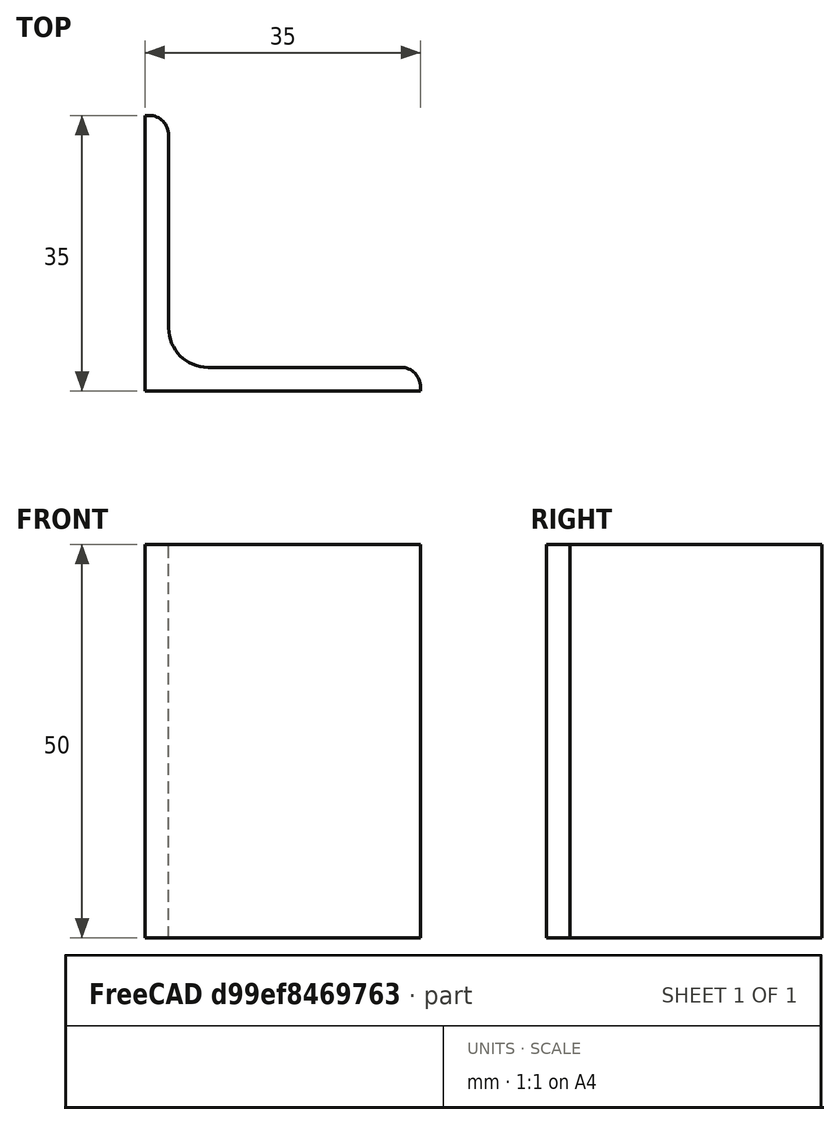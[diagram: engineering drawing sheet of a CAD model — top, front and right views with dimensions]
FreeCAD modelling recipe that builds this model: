
FCSTD DOCUMENT  (FreeCAD 0.15R4671 (Git))
Label: Angle Bar L35x35x3 EN10056 S235JR
License: All rights reserved
LicenseURL: http://en.wikipedia.org/wiki/All_rights_reserved
objects: Sketcher::SketchObject×1, Part::Extrusion×1
note: 2 computed .brp shape members not serialized (recipe doc carries the construction recipe); baked Part::Feature solids carry a one-line shape summary decoded from their .brp

FEATURE [Sketcher::SketchObject] Sketch
  sketch-geometry (9):
    g0: LineSegment StartX=0 StartY=0 StartZ=0 EndX=35 EndY=0 EndZ=0
    g1: LineSegment StartX=35 StartY=0 StartZ=0 EndX=35 EndY=0.5 EndZ=0
    g2: LineSegment StartX=32.5 StartY=3 StartZ=0 EndX=8 EndY=3 EndZ=0
    g3: LineSegment StartX=0 StartY=0 StartZ=0 EndX=0 EndY=35 EndZ=0
    g4: LineSegment StartX=0 StartY=35 StartZ=0 EndX=0.5 EndY=35 EndZ=0
    g5: LineSegment StartX=3 StartY=32.5 StartZ=0 EndX=3 EndY=8 EndZ=0
    g6: ArcOfCircle CenterX=8 CenterY=8 CenterZ=0 NormalX=0 NormalY=0 NormalZ=1 Radius=5 StartAngle=3.14159 EndAngle=4.71239
    g7: ArcOfCircle CenterX=0.5 CenterY=32.5 CenterZ=0 NormalX=0 NormalY=0 NormalZ=1 Radius=2.5 StartAngle=0 EndAngle=1.5708
    g8: ArcOfCircle CenterX=32.5 CenterY=0.5 CenterZ=0 NormalX=0 NormalY=0 NormalZ=1 Radius=2.5 StartAngle=0 EndAngle=1.5708
  constraints (23):
    c: Coincident(g0,g-1)
    c: Horizontal(g0)
    c: Coincident(g1,g0)
    c: Vertical(g1)
    c: Horizontal(g2)
    c: Coincident(g3,g-1)
    c: Vertical(g3)
    c: Coincident(g4,g3)
    c: Horizontal(g4)
    c: Vertical(g5)
    c: Tangent(g5,g6) = -1.5708
    c: Tangent(g2,g6) = 1.5708
    c: Tangent(g4,g7) = 1.5708
    c: Tangent(g5,g7) = 1.5708
    c: Tangent(g2,g8) = -1.5708
    c: Tangent(g1,g8) = -1.5708
    c: DistanceX(g0) = 35
    c: DistanceY(g3) = 35
    c: DistanceY(g0,g2) = 3
    c: DistanceX(g3,g5) = 3
    c: Radius(g6) = 5
    c: Radius(g8) = 2.5
    c: Radius(g7) = 2.5
FEATURE [Part::Extrusion] Extrude  label="Angle Bar L35x35x3 EN10056 S235JR"
  Base = -> Sketch
  Dir = (0,0,50)
  Solid = true
